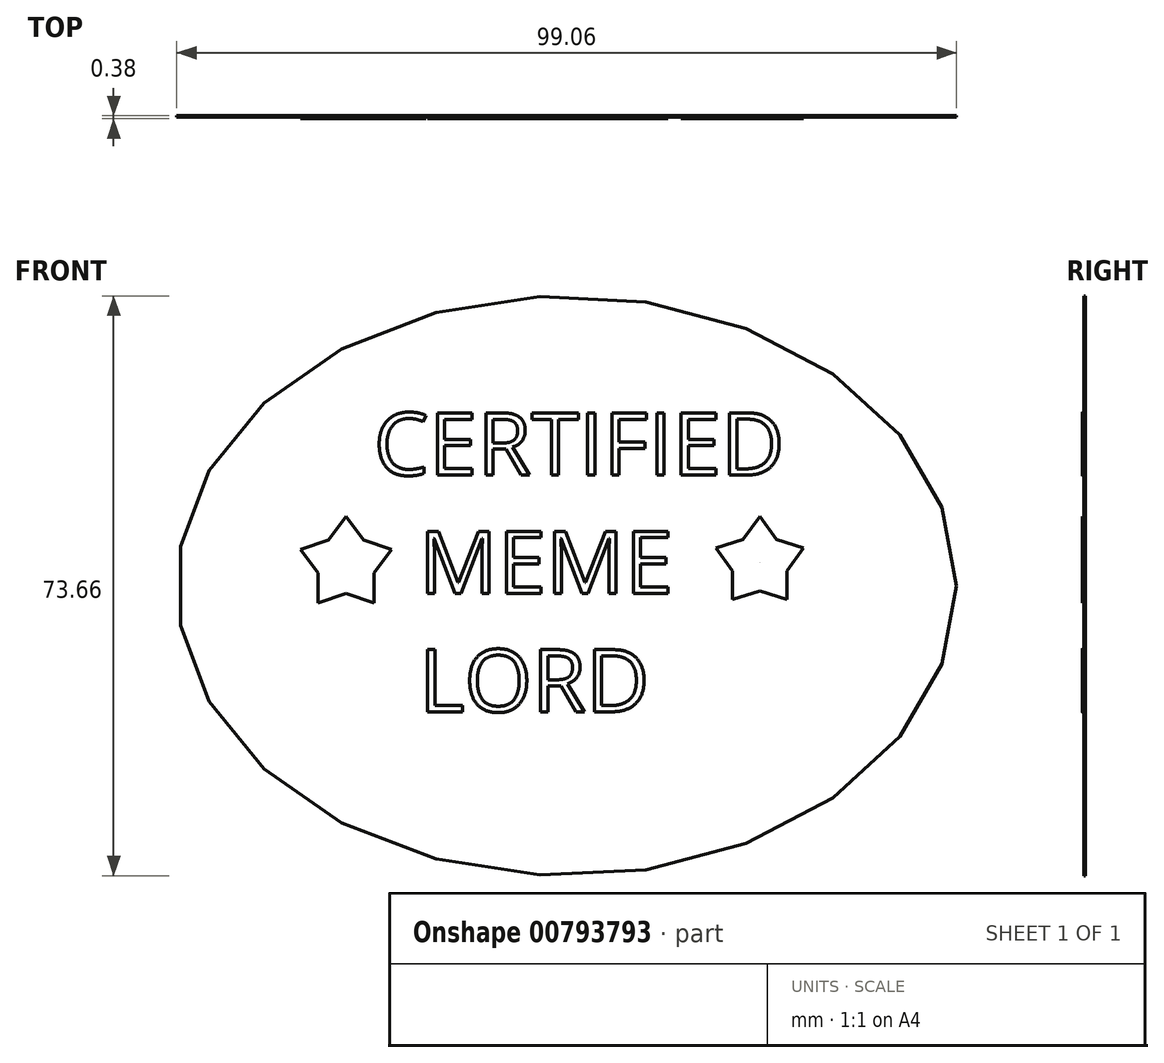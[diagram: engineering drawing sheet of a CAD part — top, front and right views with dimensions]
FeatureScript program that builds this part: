
annotation { "Feature Type Name" : "Feature", "Feature Type Description" : "" }
export const myFeature = defineFeature(function(context is Context, id is Id, definition is map)
    precondition{}
    {
        {
            var Q0;
            Q0=qCreatedBy(makeId("Front.planeOp"),FACE);
            var sketch = newSketch(context, id + "F0", { "sketchPlane" : qUnion([Q0])});
            skEllipse(sketch, "E0", {"center": v(0, 0) * mm, "majorRadius": 49.53 * mm, "minorRadius": 36.83 * mm, "majorAxis": v(1, 0)});
            skSolve(sketch);
        }
        {
            var Q0;
            Q0=makeQuery(id+"F0.imprint","IMPRINT",FACE,{"disambiguationData":[TD([[makeQuery(id+"F0.imprint","IMPRINT",EDGE,{"derivedFrom":sQuery(id+"F0.wireOp",EDGE,"E0")}),1.0]])]});
            extrude(context, id + "F1", {"entities" : qUnion([Q0]), "depth" : ((3 / 8) / 2) * mm, "offsetDistance" : 25.4 * mm});
        }
        {
            var Q0;
            Q0=makeQuery(id+"F1.opExtrude","CAP_FACE",FACE,{"disambiguationData":[OSD([sQuery(id+"F0.wireOp",EDGE,"E0")])],"isStart":false});
            var sketch = newSketch(context, id + "F2", { "sketchPlane" : qUnion([Q0])});
            skText(sketch, "E1", { "text": "CERTIFIED\n  MEME\n  LORD", "fontName": "OpenSans-Regular.ttf"});
            const initialGuessF2  = {"E1": [-0.02448, 0.01407, 1, 0, 0.00796]};
            skSetInitialGuess(sketch, initialGuessF2);
            skSolve(sketch);
        }
        {
            var Q0;
            Q0 = qSketchRegion(id + "F2", true);
            extrude(context, id + "F3", {"entities" : qUnion([Q0]), "operationType" : NewBodyOperationType.ADD, "depth" : ((3 / 8) / 2) * mm, "offsetDistance" : 25.4 * mm});
        }
        {
            var Q0;
            {var subQ0=sQuery(id+"F0.wireOp",EDGE,"E0");Q0=makeQuery(id+"F3.boolean.opBoolean","SPLIT",FACE,{"disambiguationData":[TD([makeQuery(id+"F1.opExtrude","SWEPT_FACE",FACE,{"disambiguationData":[OSD([subQ0])]})])],"derivedFrom":makeQuery(id+"F1.opExtrude","CAP_FACE",FACE,{"disambiguationData":[OSD([subQ0])],"isStart":false})});}
            var sketch = newSketch(context, id + "F4", { "sketchPlane" : qUnion([Q0])});
            skPoint(sketch, "E2", {"position": v(24.53, 2.98) * mm});
            skPoint(sketch, "E2.positionSnap0", {"position": v(-17.66, 2.98) * mm});
            skPoint(sketch, "E3", {"position": v(20.03, 1.52) * mm});
            skPoint(sketch, "E4", {"position": v(29.03, 1.52) * mm});
            skPoint(sketch, "E5", {"position": v(27.31, 6.81) * mm});
            skPoint(sketch, "E6", {"position": v(21.75, 6.81) * mm});
            skPoint(sketch, "E7", {"position": v(24.53, -1.75) * mm});
            skLineSegment(sketch, "E8", {"start": v(18.97, 4.8) * mm, "end": v(19, 4.8) * mm});
            skLineSegment(sketch, "E9", {"start": v(24.53, 2.98) * mm, "end": v(24.55, 2.99) * mm});
            skLineSegment(sketch, "E10", {"start": v(24.54, 3) * mm, "end": v(24.55, 2.99) * mm});
            skLineSegment(sketch, "E11", {"start": v(24.53, 2.98) * mm, "end": v(24.54, 3) * mm});
            skLineSegment(sketch, "E12", {"start": v(19, 4.8) * mm, "end": v(22.4, 5.91) * mm});
            skLineSegment(sketch, "E13", {"start": v(22.4, 5.91) * mm, "end": v(24.53, 8.83) * mm});
            skLineSegment(sketch, "E14", {"start": v(24.53, 8.83) * mm, "end": v(26.66, 5.9) * mm});
            skLineSegment(sketch, "E15", {"start": v(26.66, 5.9) * mm, "end": v(30.1, 4.8) * mm});
            skLineSegment(sketch, "E16", {"start": v(30.1, 4.8) * mm, "end": v(27.97, 1.87) * mm});
            skLineSegment(sketch, "E17", {"start": v(27.97, 1.87) * mm, "end": v(27.97, -1.75) * mm});
            skLineSegment(sketch, "E18", {"start": v(27.97, -1.75) * mm, "end": v(24.53, -0.63) * mm});
            skLineSegment(sketch, "E19", {"start": v(24.53, -0.63) * mm, "end": v(21.1, -1.75) * mm});
            skLineSegment(sketch, "E20", {"start": v(21.1, 1.87) * mm, "end": v(19, 4.8) * mm});
            skLineSegment(sketch, "E21", {"start": v(21.1, 1.87) * mm, "end": v(21.1, -1.75) * mm});
            skPoint(sketch, "E22", {"position": v(-28.02, 2.76) * mm});
            skLineSegment(sketch, "E23", {"start": v(-33.8, 4.64) * mm, "end": v(-30.23, 5.8) * mm});
            skLineSegment(sketch, "E24", {"start": v(-30.23, 5.8) * mm, "end": v(-28.02, 8.83) * mm});
            skLineSegment(sketch, "E25", {"start": v(-28.02, 8.83) * mm, "end": v(-25.82, 5.8) * mm});
            skLineSegment(sketch, "E26", {"start": v(-25.82, 5.8) * mm, "end": v(-22.25, 4.64) * mm});
            skLineSegment(sketch, "E27", {"start": v(-22.25, 4.64) * mm, "end": v(-24.45, 1.6) * mm});
            skLineSegment(sketch, "E28", {"start": v(-24.45, 1.6) * mm, "end": v(-24.45, -2.15) * mm});
            skLineSegment(sketch, "E29", {"start": v(-24.45, -2.15) * mm, "end": v(-28.02, -0.99) * mm});
            skLineSegment(sketch, "E30", {"start": v(-28.02, -0.99) * mm, "end": v(-31.59, -2.15) * mm});
            skLineSegment(sketch, "E31", {"start": v(-31.59, -2.15) * mm, "end": v(-31.59, 1.6) * mm});
            skLineSegment(sketch, "E32", {"start": v(-31.59, 1.6) * mm, "end": v(-33.8, 4.64) * mm});
            skSolve(sketch);
        }
        {
            var Q0;
            Q0=makeQuery(id+"F4.imprint","IMPRINT",FACE,{"disambiguationData":[TD([[makeQuery(id+"F4.imprint","IMPRINT",EDGE,{"derivedFrom":sQuery(id+"F4.wireOp",EDGE,"E9")}),-1.0]])]});
            var Q1;
            Q1=makeQuery(id+"F4.imprint","IMPRINT",FACE,{"disambiguationData":[TD([[makeQuery(id+"F4.imprint","IMPRINT",EDGE,{"derivedFrom":sQuery(id+"F4.wireOp",EDGE,"E23")}),-1.0]])]});
            extrude(context, id + "F5", {"entities" : qUnion([Q0, Q1]), "operationType" : NewBodyOperationType.ADD, "depth" : ((3 / 8) / 2) * mm, "offsetDistance" : 25.4 * mm});
        }
    });
